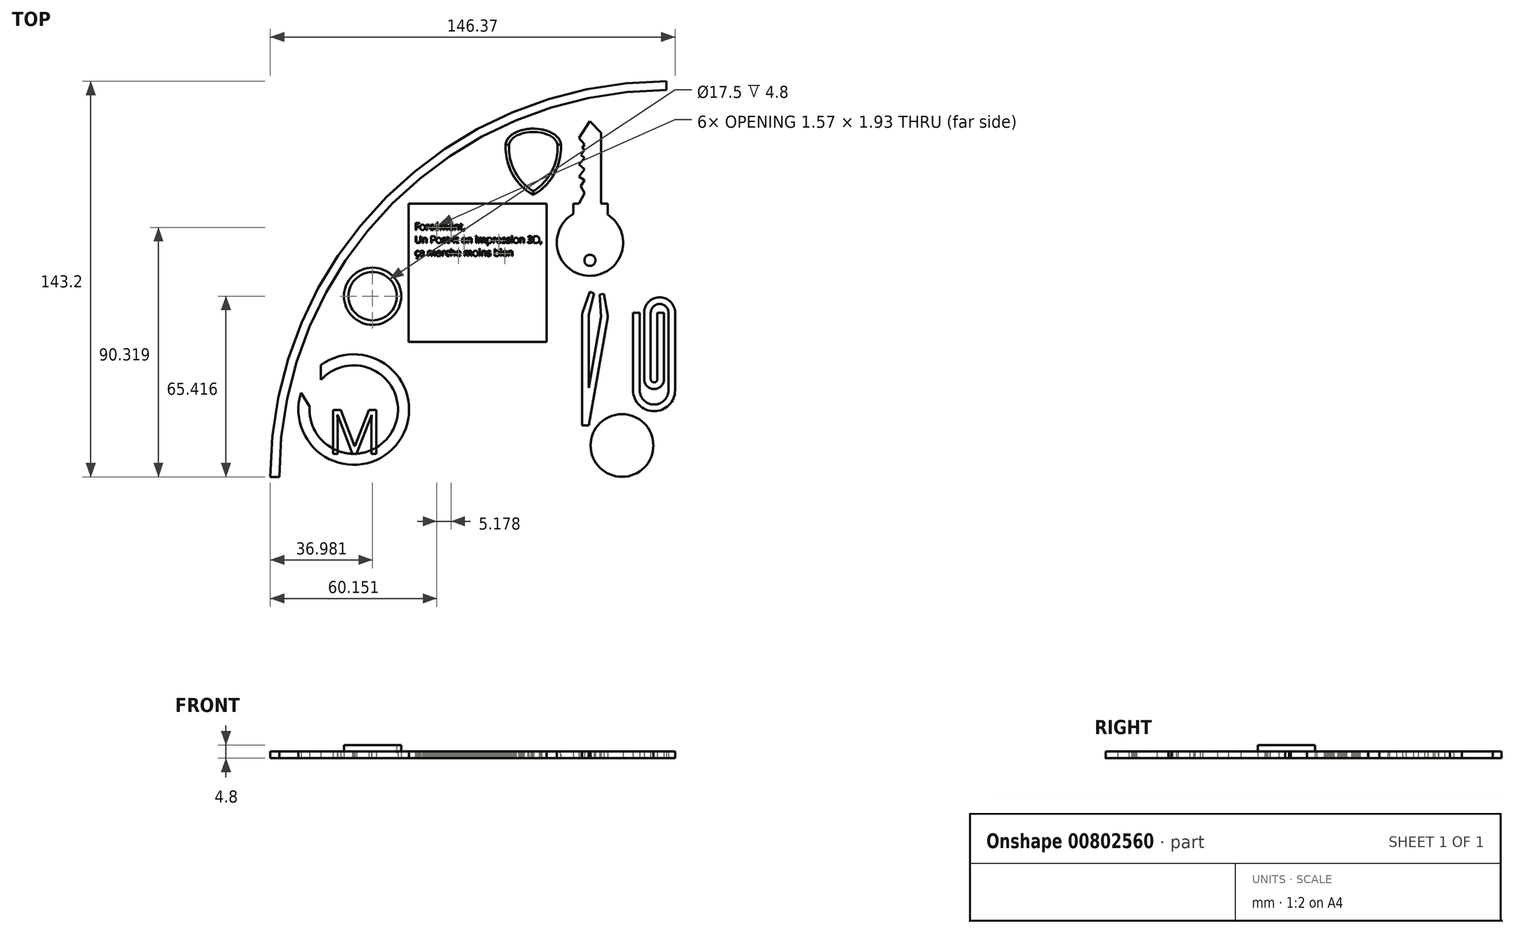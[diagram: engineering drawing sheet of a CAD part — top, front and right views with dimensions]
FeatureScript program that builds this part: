
annotation { "Feature Type Name" : "Feature", "Feature Type Description" : "" }
export const myFeature = defineFeature(function(context is Context, id is Id, definition is map)
    precondition{}
    {
        {
            var Q0;
            Q0=qCreatedBy(makeId("Top.planeOp"),FACE);
            var sketch = newSketch(context, id + "F0", { "sketchPlane" : qUnion([Q0])});
            skArc(sketch, "E0", {"start": v(69.34, 66.2) * mm, "mid": v(-29.65, 25.2) * mm, "end": v(-70.66, -73.8) * mm});
            skArc(sketch, "E1.0", {"start": v(69.34, 69.4) * mm, "mid": v(-31.91, 27.47) * mm, "end": v(-73.86, -73.8) * mm});
            skLineSegment(sketch, "E2", {"start": v(-70.66, -73.8) * mm, "end": v(-73.86, -73.8) * mm});
            skLineSegment(sketch, "E3", {"start": v(69.34, 66.2) * mm, "end": v(69.34, 69.4) * mm});
            skLineSegment(sketch, "E4.bottom", {"start": v(58.9, 56.22) * mm, "end": v(55.7, 56.22) * mm});
            skLineSegment(sketch, "E4.top", {"start": v(58.9, 24.22) * mm, "end": v(55.7, 24.22) * mm});
            skLineSegment(sketch, "E4.left", {"start": v(58.9, 56.22) * mm, "end": v(58.9, 24.22) * mm});
            skLineSegment(sketch, "E4.right", {"start": v(55.7, 56.22) * mm, "end": v(55.7, 24.22) * mm});
            skLineSegment(sketch, "E5", {"start": v(57.3, 21.02) * mm, "end": v(55.7, 24.22) * mm});
            skLineSegment(sketch, "E6", {"start": v(57.3, 21.02) * mm, "end": v(58.9, 24.22) * mm});
            skPoint(sketch, "E7.end.orphan", {"position": v(61.85, 21.02) * mm});
            skPoint(sketch, "E8.end.orphan", {"position": v(65.05, 21.02) * mm});
            skCircle(sketch, "E9", {"center": v(41.73, 11) * mm, "radius": 12 * mm});
            skCircle(sketch, "E10", {"center": v(41.73, 4.6) * mm, "radius": 2 * mm});
            skLineSegment(sketch, "E11", {"start": v(41.73, 11) * mm, "end": v(41.73, 55) * mm});
            skLineSegment(sketch, "E12", {"start": v(35.73, 25.17) * mm, "end": v(35.73, 21.4) * mm});
            skLineSegment(sketch, "E13", {"start": v(48.13, 25.17) * mm, "end": v(48.13, 21.15) * mm});
            skLineSegment(sketch, "E14", {"start": v(48.13, 25.17) * mm, "end": v(35.73, 25.17) * mm});
            skLineSegment(sketch, "E15", {"start": v(41.73, 25.17) * mm, "end": v(45.73, 25.17) * mm});
            skPoint(sketch, "E15.startSnap0", {"position": v(41.93, 25.17) * mm});
            skLineSegment(sketch, "E16", {"start": v(45.73, 25.17) * mm, "end": v(37.73, 25.17) * mm});
            skLineSegment(sketch, "E17.bottom", {"start": v(37.73, 25.17) * mm, "end": v(45.73, 25.17) * mm});
            skLineSegment(sketch, "E17.top", {"start": v(37.73, 25.17) * mm, "end": v(45.73, 25.17) * mm});
            skLineSegment(sketch, "E17.left", {"start": v(21.23, 18.77) * mm, "end": v(21.23, 18.77) * mm});
            skLineSegment(sketch, "E17.right", {"start": v(29.23, 18.77) * mm, "end": v(29.23, 18.77) * mm});
            skLineSegment(sketch, "E18", {"start": v(45.73, 25.17) * mm, "end": v(45.73, 50.72) * mm});
            skLineSegment(sketch, "E19", {"start": v(37.73, 40.09) * mm, "end": v(37.73, 39.31) * mm});
            skLineSegment(sketch, "E20", {"start": v(41.73, 55) * mm, "end": v(37.73, 48.82) * mm});
            skLineSegment(sketch, "E21", {"start": v(37.73, 48.82) * mm, "end": v(41.73, 55) * mm});
            skLineSegment(sketch, "E22", {"start": v(41.73, 55) * mm, "end": v(45.73, 50.72) * mm});
            skLineSegment(sketch, "E23", {"start": v(37.73, 48.82) * mm, "end": v(39.73, 46.63) * mm});
            skPoint(sketch, "E23.endSnap0", {"position": v(39.73, 51.91) * mm});
            skLineSegment(sketch, "E24", {"start": v(39.73, 46.63) * mm, "end": v(38.83, 45.25) * mm});
            skLineSegment(sketch, "E25", {"start": v(38.83, 45.25) * mm, "end": v(39.77, 44.64) * mm});
            skLineSegment(sketch, "E26", {"start": v(39.77, 44.64) * mm, "end": v(38.53, 42.71) * mm});
            skLineSegment(sketch, "E27", {"start": v(38.53, 42.71) * mm, "end": v(39.77, 41.6) * mm});
            skLineSegment(sketch, "E28", {"start": v(39.77, 41.6) * mm, "end": v(37.73, 39.31) * mm});
            skPoint(sketch, "E28.endSnap0", {"position": v(37.73, 40.09) * mm});
            skLineSegment(sketch, "E29", {"start": v(37.73, 39.31) * mm, "end": v(39.73, 37.53) * mm});
            skLineSegment(sketch, "E30", {"start": v(39.73, 37.53) * mm, "end": v(37.73, 34.88) * mm});
            skLineSegment(sketch, "E31", {"start": v(37.73, 34.88) * mm, "end": v(39.73, 33.59) * mm});
            skLineSegment(sketch, "E32", {"start": v(39.73, 33.59) * mm, "end": v(38.32, 31.4) * mm});
            skLineSegment(sketch, "E33", {"start": v(38.32, 31.4) * mm, "end": v(39.77, 28.88) * mm});
            skLineSegment(sketch, "E34", {"start": v(39.77, 28.88) * mm, "end": v(37.73, 25.17) * mm});
            skLineSegment(sketch, "E35", {"start": v(41.73, 25.17) * mm, "end": v(40.93, 25.17) * mm});
            skLineSegment(sketch, "E36", {"start": v(40.93, 25.17) * mm, "end": v(42.53, 25.17) * mm});
            skLineSegment(sketch, "E37", {"start": v(42.53, 25.17) * mm, "end": v(42.53, 54.15) * mm});
            skLineSegment(sketch, "E38", {"start": v(41.17, 54.15) * mm, "end": v(40.93, 25.17) * mm});
            skPoint(sketch, "E39.orphan", {"position": v(37.73, 55) * mm});
            skCircle(sketch, "E40", {"center": v(53.3, -62.4) * mm, "radius": 11.35 * mm});
            skCircle(sketch, "E41", {"center": v(-36.88, -8.37) * mm, "radius": 8.75 * mm});
            skCircle(sketch, "E42", {"center": v(-36.88, -8.37) * mm, "radius": 10.35 * mm});
            skArc(sketch, "E43", {"start": v(-59.66, -48.26) * mm, "mid": v(-28.99, -55.69) * mm, "end": v(-55.56, -38.66) * mm});
            skArc(sketch, "E44.0", {"start": v(-62.78, -43.4) * mm, "mid": v(-27.43, -61.03) * mm, "end": v(-55.56, -33.3) * mm});
            skLineSegment(sketch, "E45", {"start": v(-62.78, -43.4) * mm, "end": v(-59.66, -48.26) * mm});
            skLineSegment(sketch, "E46", {"start": v(-55.56, -33.3) * mm, "end": v(-55.56, -38.66) * mm});
            skEllipticalArc(sketch, "E47", {});
            skEllipticalArc(sketch, "E48", {});
            skPoint(sketch, "E49", {"position": v(11.23, 39.87) * mm});
            skPoint(sketch, "E50", {"position": v(12.95, 43.23) * mm});
            skPoint(sketch, "E51", {"position": v(29.5, 43.23) * mm});
            skPoint(sketch, "E52", {"position": v(31.23, 39.87) * mm});
            skEllipticalArc(sketch, "E53.trimOffspring", {});
            skLineSegment(sketch, "E54.bottom", {"start": v(26.09, 25.12) * mm, "end": v(-23.91, 25.12) * mm});
            skLineSegment(sketch, "E54.top", {"start": v(26.09, -24.88) * mm, "end": v(-23.91, -24.88) * mm});
            skLineSegment(sketch, "E54.left", {"start": v(26.09, 25.12) * mm, "end": v(26.09, -24.88) * mm});
            skLineSegment(sketch, "E54.right", {"start": v(-23.91, 25.12) * mm, "end": v(-23.91, -24.88) * mm});
            skText(sketch, "E55", { "text": "Forcément, \nUn Post-It en impression 3D,\nça marche moins bien", "fontName": "OpenSans-Regular.ttf"});
            skLineSegment(sketch, "E56.left", {"start": v(38.83, -15.16) * mm, "end": v(38.83, -55.16) * mm});
            skLineSegment(sketch, "E56.right", {"start": v(41.23, -15.16) * mm, "end": v(41.23, -41.55) * mm});
            skLineSegment(sketch, "E57.left", {"start": v(45.78, -15.77) * mm, "end": v(41.23, -41.55) * mm});
            skLineSegment(sketch, "E57.right", {"start": v(48.14, -16.18) * mm, "end": v(41.27, -55.16) * mm});
            skLineSegment(sketch, "E58", {"start": v(45.18, -7.75) * mm, "end": v(46.75, -7.47) * mm});
            skLineSegment(sketch, "E59", {"start": v(46.75, -7.47) * mm, "end": v(48.14, -15.35) * mm});
            skLineSegment(sketch, "E60", {"start": v(45.18, -7.75) * mm, "end": v(45.78, -15.77) * mm});
            skLineSegment(sketch, "E61", {"start": v(48.14, -15.35) * mm, "end": v(48.14, -16.18) * mm});
            skLineSegment(sketch, "E62", {"start": v(38.98, -14.34) * mm, "end": v(41.71, -6.82) * mm});
            skLineSegment(sketch, "E63", {"start": v(41.71, -6.82) * mm, "end": v(43.22, -7.37) * mm});
            skLineSegment(sketch, "E64", {"start": v(43.22, -7.37) * mm, "end": v(41.23, -15.16) * mm});
            skLineSegment(sketch, "E65", {"start": v(38.98, -14.34) * mm, "end": v(38.83, -15.16) * mm});
            skLineSegment(sketch, "E66", {"start": v(38.83, -55.16) * mm, "end": v(41.27, -55.16) * mm});
            skLineSegment(sketch, "E67.bottom", {"start": v(61.3, -14.39) * mm, "end": v(63.7, -14.39) * mm});
            skLineSegment(sketch, "E67.left", {"start": v(61.3, -14.39) * mm, "end": v(61.3, -38.39) * mm});
            skLineSegment(sketch, "E67.right", {"start": v(63.7, -14.39) * mm, "end": v(63.7, -38.39) * mm});
            skLineSegment(sketch, "E68.bottom", {"start": v(70.1, -14.39) * mm, "end": v(72.5, -14.39) * mm});
            skLineSegment(sketch, "E68.top", {"start": v(70.1, -42.39) * mm, "end": v(72.5, -42.39) * mm});
            skLineSegment(sketch, "E68.left", {"start": v(70.1, -14.39) * mm, "end": v(70.1, -42.39) * mm});
            skLineSegment(sketch, "E68.right", {"start": v(72.5, -14.39) * mm, "end": v(72.5, -42.39) * mm});
            skArc(sketch, "E69", {"start": v(70.1, -14.39) * mm, "mid": v(66.9, -11.19) * mm, "end": v(63.7, -14.39) * mm});
            skArc(sketch, "E70.0", {"start": v(72.5, -14.39) * mm, "mid": v(66.9, -8.79) * mm, "end": v(61.3, -14.39) * mm});
            skLineSegment(sketch, "E71.bottom", {"start": v(57.3, -14.39) * mm, "end": v(59.7, -14.39) * mm});
            skLineSegment(sketch, "E71.top", {"start": v(57.3, -42.39) * mm, "end": v(59.7, -42.39) * mm});
            skLineSegment(sketch, "E71.left", {"start": v(57.3, -14.39) * mm, "end": v(57.3, -42.39) * mm});
            skLineSegment(sketch, "E71.right", {"start": v(59.7, -14.39) * mm, "end": v(59.7, -42.39) * mm});
            skArc(sketch, "E72", {"start": v(59.7, -42.39) * mm, "mid": v(64.9, -47.59) * mm, "end": v(70.1, -42.39) * mm});
            skArc(sketch, "E73.0", {"start": v(57.3, -42.39) * mm, "mid": v(64.9, -49.99) * mm, "end": v(72.5, -42.39) * mm});
            skText(sketch, "E74", { "text": "M", "fontName": "OpenSans-Regular.ttf"});
            skPoint(sketch, "E75.end.orphan", {"position": v(-30.09, -34.76) * mm});
            skArc(sketch, "E76", {"start": v(-16.35, -48.26) * mm, "mid": v(14.33, -55.69) * mm, "end": v(-12.25, -38.66) * mm});
            skArc(sketch, "E77.0", {"start": v(-19.46, -43.4) * mm, "mid": v(15.89, -61.03) * mm, "end": v(-12.25, -33.3) * mm});
            skLineSegment(sketch, "E78", {"start": v(-19.46, -43.4) * mm, "end": v(-16.35, -48.26) * mm});
            skLineSegment(sketch, "E79", {"start": v(-12.25, -33.3) * mm, "end": v(-12.25, -38.66) * mm});
            skText(sketch, "E80", { "text": "M", "fontName": "OpenSans-Regular.ttf"});
            skPoint(sketch, "E81.end.orphan", {"position": v(13.23, -34.76) * mm});
            skLineSegment(sketch, "E82", {"start": v(61.3, -38.39) * mm, "end": v(63.7, -38.39) * mm});
            skPoint(sketch, "E67.top.start.orphan", {"position": v(61.3, -42.39) * mm});
            skLineSegment(sketch, "E83.bottom", {"start": v(66.1, -14.39) * mm, "end": v(68.5, -14.39) * mm});
            skLineSegment(sketch, "E83.left", {"start": v(66.1, -14.39) * mm, "end": v(66.1, -38.39) * mm});
            skLineSegment(sketch, "E83.right", {"start": v(68.5, -14.39) * mm, "end": v(68.5, -38.39) * mm});
            skLineSegment(sketch, "E84", {"start": v(66.1, -38.39) * mm, "end": v(68.5, -38.39) * mm});
            skArc(sketch, "E85", {"start": v(63.7, -38.39) * mm, "mid": v(64.9, -39.59) * mm, "end": v(66.1, -38.39) * mm});
            skArc(sketch, "E86.0", {"start": v(61.3, -38.39) * mm, "mid": v(64.9, -41.99) * mm, "end": v(68.5, -38.39) * mm});
            skLineSegment(sketch, "E87", {"start": v(-51.19, -49.53) * mm, "end": v(-48.4, -49.53) * mm});
            skLineSegment(sketch, "E88", {"start": v(-48.4, -49.53) * mm, "end": v(-43.38, -62.62) * mm});
            skLineSegment(sketch, "E89", {"start": v(-43.38, -62.62) * mm, "end": v(-43.3, -62.62) * mm});
            skLineSegment(sketch, "E90", {"start": v(-43.3, -62.62) * mm, "end": v(-38.23, -49.55) * mm});
            skLineSegment(sketch, "E91", {"start": v(-38.23, -49.55) * mm, "end": v(-35.48, -49.55) * mm});
            const initialGuessF0  = {"E47": [0.021226862445473664, 0.04626882898807526, 1, 0, 0.01, 0.006, 0, 3.141592653589793], "E48": [0.011226862445473662, 0.04626882898807526, 0.48564293117863244, -0.8741572761215376, 0.02059126028197401, 0.01982755325631149, 0, 1.0929807321065532], "E53.trimOffspring": [0.031226862445473666, 0.04626882898807526, -0.4856429311786319, -0.8741572761215379, 0.020591260281974, 0.01982755325631149, 5.190204575073031, 0], "E55": [-0.02165, 0.0156, 1, 0, 0.0025], "E74": [-0.05337, -0.0654, 1, 0, 0.016], "E80": [-0.01005, -0.0654, 1, 0, 0.016]};
            skSetInitialGuess(sketch, initialGuessF0);
            skSolve(sketch);
        }
        {
            var Q0;
            {var subQ1=sQuery(id+"F0.wireOp",EDGE,"E47");var subQ4=sQuery(id+"F0.wireOp",EDGE,"E48");var subQ6=makeQuery(id+"F0.imprint","INTERSECT",VERTEX,{"disambiguationData":[OD(1.0)],"derivedFrom":[subQ1,subQ4]});Q0=makeQuery(id+"F0.imprint","IMPRINT",FACE,{"disambiguationData":[TD([[makeQuery(id+"F0.imprint","IMPRINT",EDGE,{"disambiguationData":[TD([[subQ6,-1.0]])],"derivedFrom":subQ1}),1.0]])]});}
            var Q1;
            Q1=makeQuery(id+"F0.imprint","IMPRINT",FACE,{"disambiguationData":[TD([[makeQuery(id+"F0.imprint","IMPRINT",EDGE,{"derivedFrom":sQuery(id+"F0.wireOp",EDGE,"E0")}),-1.0]])]});
            var Q2;
            Q2=makeQuery(id+"F0.imprint","IMPRINT",FACE,{"disambiguationData":[TD([[makeQuery(id+"F0.imprint","IMPRINT",EDGE,{"derivedFrom":sQuery(id+"F0.wireOp",EDGE,"E56.left")}),1.0]])]});
            var Q3;
            Q3=makeQuery(id+"F0.imprint","IMPRINT",FACE,{"disambiguationData":[TD([[makeQuery(id+"F0.imprint","IMPRINT",EDGE,{"derivedFrom":sQuery(id+"F0.wireOp",EDGE,"E71.bottom")}),-1.0]])]});
            var Q4;
            Q4=makeQuery(id+"F0.imprint","IMPRINT",FACE,{"disambiguationData":[TD([[makeQuery(id+"F0.imprint","IMPRINT",EDGE,{"derivedFrom":sQuery(id+"F0.wireOp",EDGE,"E68.top")}),-1.0]])]});
            var Q5;
            Q5=makeQuery(id+"F0.imprint","IMPRINT",FACE,{"disambiguationData":[TD([[makeQuery(id+"F0.imprint","IMPRINT",EDGE,{"derivedFrom":sQuery(id+"F0.wireOp",EDGE,"E68.bottom")}),-1.0]])]});
            var Q6;
            Q6=makeQuery(id+"F0.imprint","IMPRINT",FACE,{"disambiguationData":[TD([[makeQuery(id+"F0.imprint","IMPRINT",EDGE,{"derivedFrom":sQuery(id+"F0.wireOp",EDGE,"E67.bottom")}),1.0]])]});
            var Q7;
            Q7=makeQuery(id+"F0.imprint","IMPRINT",FACE,{"disambiguationData":[TD([[makeQuery(id+"F0.imprint","IMPRINT",EDGE,{"derivedFrom":sQuery(id+"F0.wireOp",EDGE,"E67.bottom")}),-1.0]])]});
            var Q8;
            Q8=makeQuery(id+"F0.imprint","IMPRINT",FACE,{"disambiguationData":[TD([[makeQuery(id+"F0.imprint","IMPRINT",EDGE,{"derivedFrom":sQuery(id+"F0.wireOp",EDGE,"E40")}),1.0]])]});
            var Q9;
            Q9=makeQuery(id+"F0.imprint","IMPRINT",FACE,{"disambiguationData":[TD([[makeQuery(id+"F0.imprint","IMPRINT",EDGE,{"derivedFrom":sQuery(id+"F0.wireOp",EDGE,"E54.bottom")}),1.0]])]});
            var Q10;
            Q10=makeQuery(id+"F0.imprint","IMPRINT",FACE,{"disambiguationData":[TD([[makeQuery(id+"F0.imprint","IMPRINT",EDGE,{"derivedFrom":sQuery(id+"F0.wireOp",EDGE,"E82")}),-1.0]])]});
            var Q11;
            Q11=makeQuery(id+"F0.imprint","IMPRINT",FACE,{"disambiguationData":[TD([[makeQuery(id+"F0.imprint","IMPRINT",EDGE,{"derivedFrom":sQuery(id+"F0.wireOp",EDGE,"E83.bottom")}),-1.0]])]});
            extrude(context, id + "F1", {"entities" : qUnion([Q0, Q1, Q2, Q3, Q4, Q5, Q6, Q7, Q8, Q9, Q10, Q11]), "depth" : 2.4 * mm, "offsetDistance" : 25 * mm});
        }
        {
            var Q0;
            Q0=makeQuery(id+"F1.opExtrude","CAP_EDGE",EDGE,{"disambiguationData":[OSD([sQuery(id+"F0.wireOp",EDGE,"E48")])],"isStart":false});
            var Q1;
            Q1=makeQuery(id+"F1.opExtrude","CAP_EDGE",EDGE,{"disambiguationData":[OSD([sQuery(id+"F0.wireOp",EDGE,"E53.trimOffspring")])],"isStart":false});
            var Q2;
            Q2=makeQuery(id+"F1.opExtrude","CAP_EDGE",EDGE,{"disambiguationData":[OSD([sQuery(id+"F0.wireOp",EDGE,"E47")])],"isStart":false});
            fillet(context, id + "F2", {"entities" : qUnion([Q0, Q1, Q2]), "radius" : 1.2 * mm, "tangentPropagation" : true, "allowEdgeOverflow" : false});
        }
        {
            var Q0;
            {var subQ3=sQuery(id+"F0.wireOp",EDGE,"E23");Q0=makeQuery(id+"F0.imprint","IMPRINT",FACE,{"disambiguationData":[TD([[makeQuery(id+"F0.imprint","IMPRINT",EDGE,{"derivedFrom":subQ3}),1.0]])]});}
            var Q1;
            {var subQ0=sQuery(id+"F0.wireOp",EDGE,"E18");Q1=makeQuery(id+"F0.imprint","IMPRINT",FACE,{"disambiguationData":[TD([[makeQuery(id+"F0.imprint","IMPRINT",EDGE,{"derivedFrom":subQ0}),1.0]])]});}
            var Q2;
            {var subQ1=sQuery(id+"F0.wireOp",EDGE,"E12");Q2=makeQuery(id+"F0.imprint","IMPRINT",FACE,{"disambiguationData":[TD([[makeQuery(id+"F0.imprint","IMPRINT",EDGE,{"derivedFrom":subQ1}),1.0]])]});}
            var Q3;
            {var subQ1=sQuery(id+"F0.wireOp",EDGE,"E13");Q3=makeQuery(id+"F0.imprint","IMPRINT",FACE,{"disambiguationData":[TD([[makeQuery(id+"F0.imprint","IMPRINT",EDGE,{"derivedFrom":subQ1}),-1.0]])]});}
            var Q4;
            Q4=makeQuery(id+"F0.imprint","IMPRINT",FACE,{"disambiguationData":[TD([[makeQuery(id+"F0.imprint","IMPRINT",EDGE,{"derivedFrom":sQuery(id+"F0.wireOp",EDGE,"E10")}),-1.0]])]});
            var Q5;
            {var subQ5=sQuery(id+"F0.wireOp",EDGE,"E37");Q5=makeQuery(id+"F0.imprint","IMPRINT",FACE,{"disambiguationData":[TD([[makeQuery(id+"F0.imprint","IMPRINT",EDGE,{"derivedFrom":subQ5}),1.0]])]});}
            var Q6;
            {var subQ5=sQuery(id+"F0.wireOp",EDGE,"E38");Q6=makeQuery(id+"F0.imprint","IMPRINT",FACE,{"disambiguationData":[TD([[makeQuery(id+"F0.imprint","IMPRINT",EDGE,{"derivedFrom":subQ5}),1.0]])]});}
            extrude(context, id + "F3", {"entities" : qUnion([Q0, Q1, Q2, Q3, Q4, Q5, Q6]), "depth" : 2.4 * mm, "offsetDistance" : 25 * mm});
        }
        {
            var Q0;
            Q0=makeQuery(id+"F0.imprint","IMPRINT",FACE,{"disambiguationData":[TD([[makeQuery(id+"F0.imprint","IMPRINT",EDGE,{"derivedFrom":sQuery(id+"F0.wireOp",EDGE,"E41")}),-1.0]])]});
            extrude(context, id + "F4", {"entities" : qUnion([Q0]), "depth" : 4.8 * mm, "offsetDistance" : 25 * mm});
        }
        {
            var Q0;
            {var subQ7=sQuery(id+"F0.wireOp",EDGE,"E74.sketch_text.stroke-1");Q0=makeQuery(id+"F0.imprint","IMPRINT",FACE,{"disambiguationData":[TD([[makeQuery(id+"F0.imprint","IMPRINT",EDGE,{"derivedFrom":subQ7}),-1.0]])]});}
            var Q1;
            Q1=makeQuery(id+"F0.imprint","IMPRINT",FACE,{"disambiguationData":[TD([[makeQuery(id+"F0.imprint","IMPRINT",EDGE,{"derivedFrom":sQuery(id+"F0.wireOp",EDGE,"E44.0")}),1.0]])]});
            extrude(context, id + "F5", {"entities" : qUnion([Q0, Q1]), "depth" : 2.4 * mm, "offsetDistance" : 25 * mm});
        }
    });
